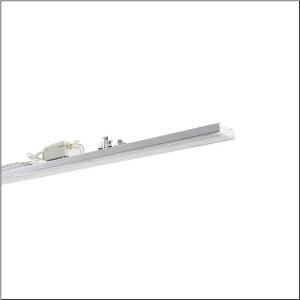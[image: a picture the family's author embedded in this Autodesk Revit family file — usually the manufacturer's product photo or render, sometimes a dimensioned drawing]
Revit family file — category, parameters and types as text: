
# Revit family: licross_r__21_recessed_mo_52te107n485g_2b82
name_source: partatom
category: Lighting Fixtures
units: mm (PartAtom-declared; Revit-internal decimal feet)

## family parameters
Cut with Voids When Loaded = No
Host = Face
Light Source = No
Part Type = Normal
Room Calculation Point = No
Round Connector Dimension = Use Diameter
Shared = No

## types (1)
- Licross® 21 Recessed MO (1 x LED, 8580 lm, 47.9 W, 4000K)
    Apparent Load = 48 VA
    CIE Flux Codes = 50 81 96 100 100
    Color Rendering = 80
    Color Temperature = 4000K
    Default Elevation = 1800 mm
    Description = Licross® 21 Recessed MO, luminaire insert, of sheet steel, galvanised, coil coated, white, length: 1.500mm, width: 66mm, height: 67mm, LED rated luminous flux: 8.560lm, light colour: 840, control gear: ON/OFF, with plug, 3-pole, with phase selection, mains connection: 220..240V, AC, 50/60Hz, rated input power: 48W, halogen-free wiring, primary optical cover: cover, of PMMA, light emission: direct distribution, primary light characteristic: symmetric, protection rating (complete): IP54, insulation class (complete): insulation class I (protective earthing), certification: CE, ENEC, VDE, UKCA, protection symbol: D if used in an environment with non-conductive dust loads with corresponding accessories, impact resistance: IK06, permissible ambient temperature for indoor applications: -35..+40°C, corresponds to IFS (International Featured Standards) requirements for safety and quality in the food industry, reducing of maximum allowable ambient temperature of 5°C with ceiling mounting, LABS conformity tested according to VDMA 24364:2018-05, packaging unit: 1 piece
    Height = 58 mm
    Lamp = 1 x LED
    Lamp Light Flux = 8580 lm
    Lamp Power = 47.9 W
    Lamp count = 1
    Length = 1500 mm
    Luminous efficacy = 179 lm/W
    Manufacturer = Siteco
    ModVariant = No
    Model = 52TE107N485G
    Mounting Place = Ceiling
    Mounting Type = Pendant
    Number of Poles = 1
    OnlyDefault = Yes
    Power Factor = 1
    Product Name = Licross® 21 Recessed MO
    Product group = luminaire insert
    ProductGroupID = 901
    Protection Class = Protection class I
    Protection Degree = IP 54
    RLX_Detail_Level = 1
    RLX_Emergency_Light_Flux = 0 lm
    RLX_Emergency_Type = 0
    RLX_Emergency_Type_DB = No
    RlxData = <blob elided: 20741 chars, md5=795112d6>
    Socket = socket
    Standby Power = 0 W
    System Light Flux = 8580 lm
    System Power = 48 W
    Type Comments = Product without accessories
    Type Image = l_1296930.jpg
    URL = http://relux.com
    VarID = ---
    Voltage = 0 V
    Weight = 0.00 kg
    Width = 66 mm

## geometry (parser evidence)
native form markers: Blend x4, Sweep x13
no freeform markers — native parametric forms only
